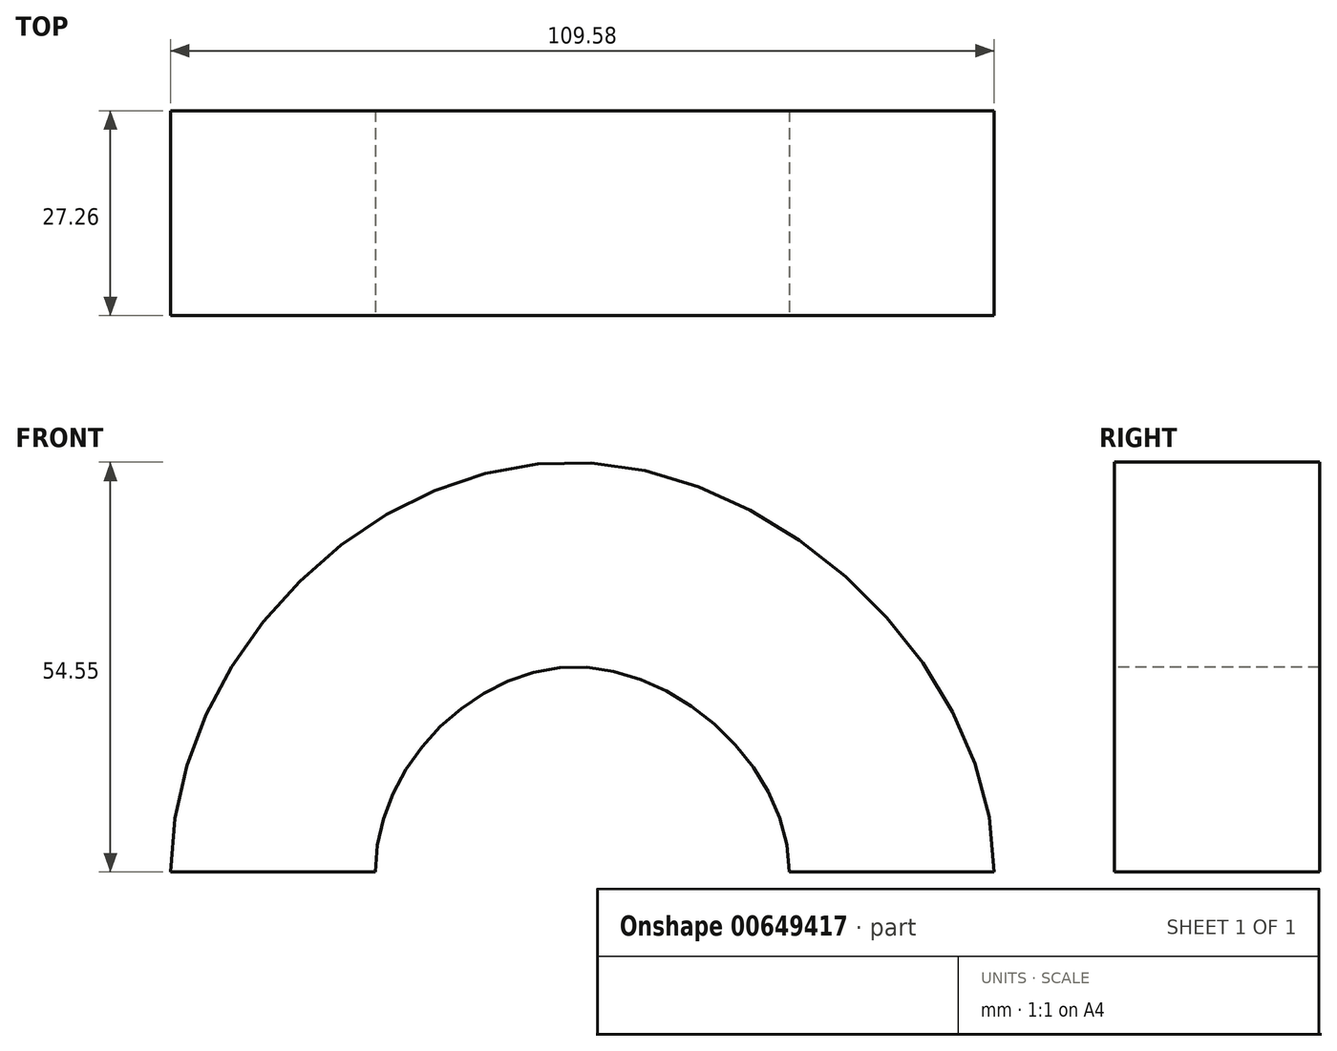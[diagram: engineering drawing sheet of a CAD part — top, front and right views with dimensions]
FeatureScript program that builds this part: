
annotation { "Feature Type Name" : "Feature", "Feature Type Description" : "" }
export const myFeature = defineFeature(function(context is Context, id is Id, definition is map)
    precondition{}
    {
        {
            var Q0;
            Q0=qCreatedBy(makeId("Top.planeOp"),FACE);
            var sketch = newSketch(context, id + "F0", { "sketchPlane" : qUnion([Q0])});
            skLineSegment(sketch, "E0.bottom", {"start": v(-54.79, 0) * mm, "end": v(-27.53, 0) * mm});
            skLineSegment(sketch, "E0.top", {"start": v(-54.79, -27.26) * mm, "end": v(-27.53, -27.26) * mm});
            skLineSegment(sketch, "E0.left", {"start": v(-54.79, 0) * mm, "end": v(-54.79, -27.26) * mm});
            skLineSegment(sketch, "E0.right", {"start": v(-27.53, 0) * mm, "end": v(-27.53, -27.26) * mm});
            skPoint(sketch, "E1", {"position": v(-54.79, -13.63) * mm});
            skPoint(sketch, "E2", {"position": v(-41.16, -13.63) * mm});
            skLineSegment(sketch, "E3", {"start": v(0, 0) * mm, "end": v(0, -27.26) * mm});
            skPoint(sketch, "E4.MirrorP", {"position": v(41.16, -13.63) * mm});
            skLineSegment(sketch, "E5.MirrorCS", {"start": v(54.79, 0) * mm, "end": v(27.53, 0) * mm});
            skPoint(sketch, "E6.MirrorP", {"position": v(54.79, -13.63) * mm});
            skLineSegment(sketch, "E7.MirrorCS", {"start": v(27.53, 0) * mm, "end": v(27.53, -27.26) * mm});
            skLineSegment(sketch, "E8.MirrorCS", {"start": v(54.79, 0) * mm, "end": v(54.79, -27.26) * mm});
            skLineSegment(sketch, "E9.MirrorCS", {"start": v(54.79, -27.26) * mm, "end": v(27.53, -27.26) * mm});
            skSolve(sketch);
        }
        {
            var Q0;
            Q0=sQuery(id+"F0.wireOp",EDGE,"E3");
            cPlane(context, id + "F1", {"entities" : qUnion([Q0]), "cplaneType" : CPlaneType.LINE_ANGLE, "offset" : 25 * mm, "angle" : 90 * degree, "width" : 150 * mm, "height" : 150 * mm});
        }
        {
            var Q0;
            Q0=qCreatedBy(id+"F1.planeOp",FACE);
            var sketch = newSketch(context, id + "F2", { "sketchPlane" : qUnion([Q0])});
            skLineSegment(sketch, "E10.0", {"start": v(0, 0) * mm, "end": v(-27.26, 0) * mm});
            skLineSegment(sketch, "E11", {"start": v(0, 0) * mm, "end": v(0, 27.26) * mm});
            skLineSegment(sketch, "E12.bottom", {"start": v(0, 27.26) * mm, "end": v(-27.26, 27.26) * mm});
            skLineSegment(sketch, "E12.top", {"start": v(0, 54.52) * mm, "end": v(-27.26, 54.52) * mm});
            skLineSegment(sketch, "E12.left", {"start": v(0, 27.26) * mm, "end": v(0, 54.52) * mm});
            skLineSegment(sketch, "E12.right", {"start": v(-27.26, 27.26) * mm, "end": v(-27.26, 54.52) * mm});
            skSolve(sketch);
        }
        {
            var Q0;
            Q0=sQuery(id+"F0.wireOp",EDGE,"E0.top");
            cPlane(context, id + "F3", {"entities" : qUnion([Q0]), "cplaneType" : CPlaneType.LINE_ANGLE, "offset" : 25 * mm, "angle" : 0 * degree, "width" : 150 * mm, "height" : 150 * mm});
        }
        {
            var Q0;
            Q0=qCreatedBy(id+"F3.planeOp",FACE);
            var sketch = newSketch(context, id + "F4", { "sketchPlane" : qUnion([Q0])});
            skLineSegment(sketch, "E13.0", {"start": v(54.79, 0) * mm, "end": v(27.53, 0) * mm});
            skLineSegment(sketch, "E14.0", {"start": v(-54.79, 0) * mm, "end": v(-27.53, 0) * mm});
            skArc(sketch, "E15", {"start": v(27.53, 0) * mm, "mid": v(0, 27.26) * mm, "end": v(-27.53, 0) * mm});
            skLineSegment(sketch, "E16.0", {"start": v(0, 27.26) * mm, "end": v(0, 54.52) * mm});
            skSolve(sketch);
        }
        {
            var Q0;
            Q0=makeQuery(id+"F0.imprint","IMPRINT",FACE,{"disambiguationData":[TD([[makeQuery(id+"F0.imprint","IMPRINT",EDGE,{"derivedFrom":sQuery(id+"F0.wireOp",EDGE,"E0.bottom")}),-1.0]])]});
            var Q1;
            Q1=makeQuery(id+"F2.imprint","IMPRINT",FACE,{"disambiguationData":[TD([[makeQuery(id+"F2.imprint","IMPRINT",EDGE,{"derivedFrom":sQuery(id+"F2.wireOp",EDGE,"E12.bottom")}),-1.0]])]});
            var Q2;
            Q2=makeQuery(id+"F0.imprint","IMPRINT",FACE,{"disambiguationData":[TD([[makeQuery(id+"F0.imprint","IMPRINT",EDGE,{"derivedFrom":sQuery(id+"F0.wireOp",EDGE,"E5.MirrorCS")}),1.0]])]});
            var Q3;
            Q3=sQuery(id+"F4.wireOp",EDGE,"E15");
            var Q4;
            Q4=sQuery(id+"F4.wireOp",VERTEX,"E13.0.start");
            var Q5;
            Q5=sQuery(id+"F2.wireOp",VERTEX,"E12.right.end");
            var Q6;
            Q6=sQuery(id+"F4.wireOp",VERTEX,"E14.0.start");
            loft(context, id + "F5", {"startCondition" : LoftEndDerivativeType.NORMAL_TO_PROFILE, "startMagnitude" : 1, "endCondition" : LoftEndDerivativeType.NORMAL_TO_PROFILE, "endMagnitude" : 1, "sheetProfilesArray" : [{ "sheetProfileEntities" : qUnion([Q0]) }, { "sheetProfileEntities" : qUnion([Q1]) }, { "sheetProfileEntities" : qUnion([Q2]) }], "guidesArray" : [{ "guideEntities" : qUnion([Q3]), "guideDerivativeType" : LoftGuideDerivativeType.DEFAULT, "guideDerivativeMagnitude" : 1 }], "connections" : [{ "connectionEntities" : qUnion([Q4, Q5, Q6]), "connectionEdgeQueries" : qUnion([]), "connectionEdgeParameters" : [] }]});
        }
    });
